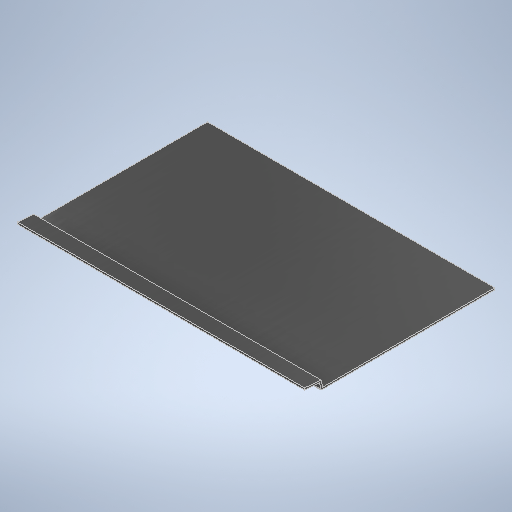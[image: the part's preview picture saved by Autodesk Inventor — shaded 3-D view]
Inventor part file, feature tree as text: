
AUTODESK INVENTOR PART (.ipt)
format: ipt  version: 2025.1 (Build 291241020, 241B)  size: 283,648 bytes
history: native  units: in
note: dims shown in document units (in); Inventor stores cm internally (conversion verified against a paired STEP export)
features: extrude x1, sketch x1
ambient origin geometry x8: Origin, YZ Plane, XZ Plane, XY Plane, X Axis, Y Axis, Z Axis, Center Point
bodies: Body1 (feature_tree)
feature tree (2):
  extrude  "Extrusion4"  Depth=0.125in
  sketch  "Sketch1"  dims[d0=23.408in d1=0.125in d2=0.265in d7=0.125in d8=0.237in d9=1.1431in d10=0.125in d11=0.7449in d12=0.125in d13=12.09in d18=0.125in d20=12.0907in d21=0.3425in d22=0.125in d23=0.125in d24=0.1549in d25=0.661in d28=0.125in d29=0.1254in d30=0.125in d32=0.125in d33=0.125in d34=5.625in d35=6.6451in d36=0.4476in d37=0.0449in d38=6.112in d41=0.125in d42=0.125in d43=0.125in d44=5.625in d45=11.655in d46=1.1103in d47=0.4636in d48=0.0215in d49=19.45in d50=0.0in]
